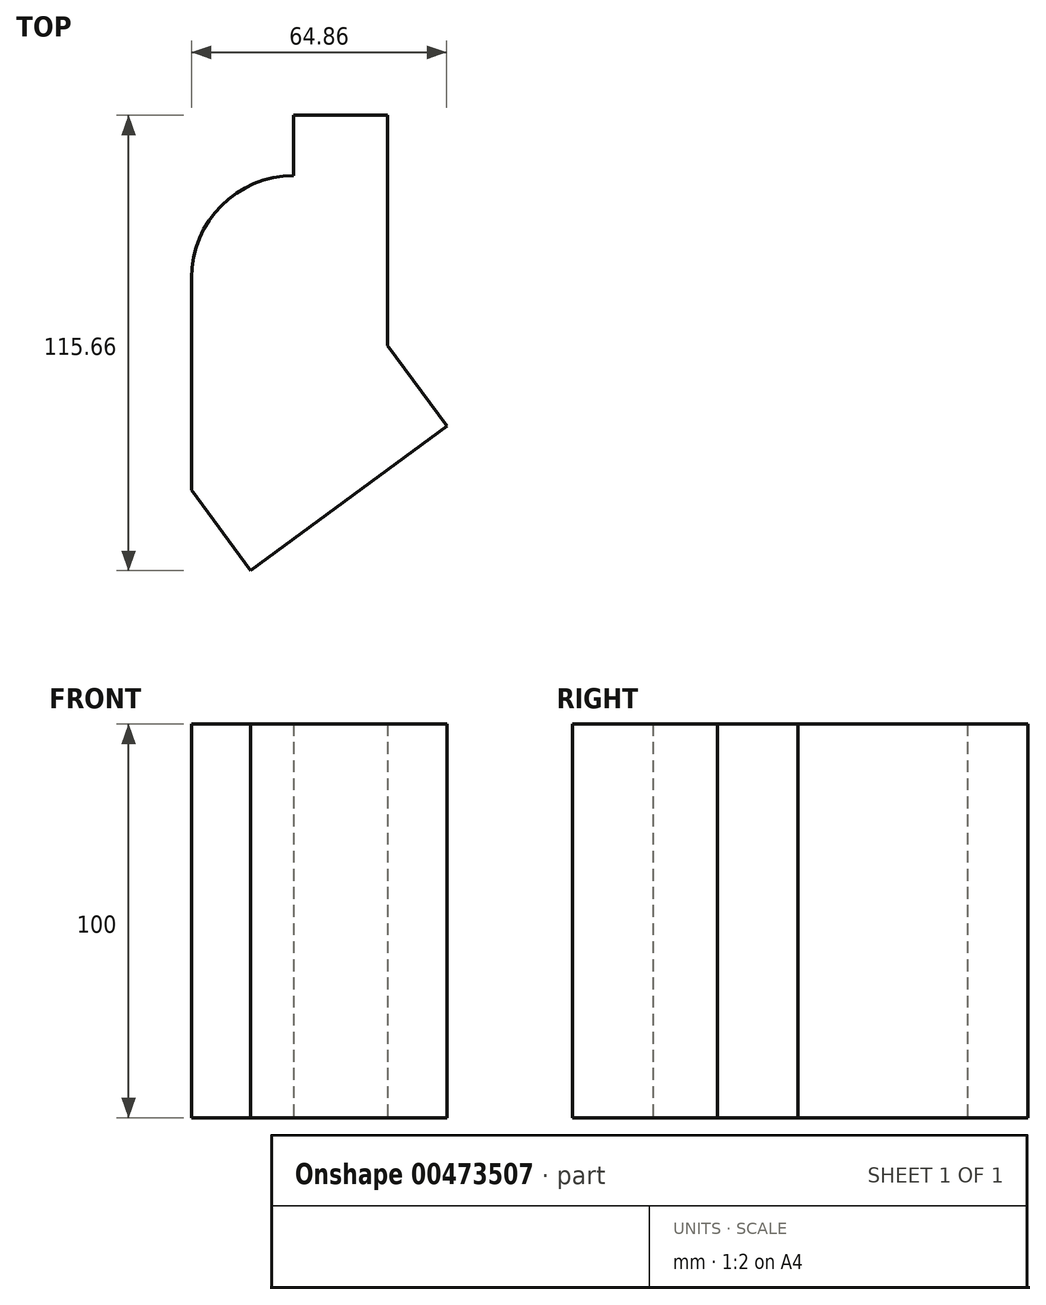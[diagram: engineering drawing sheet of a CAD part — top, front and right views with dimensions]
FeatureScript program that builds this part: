
annotation { "Feature Type Name" : "Feature", "Feature Type Description" : "" }
export const myFeature = defineFeature(function(context is Context, id is Id, definition is map)
    precondition{}
    {
        {
            var Q0;
            Q0=qCreatedBy(makeId("Top.planeOp"),FACE);
            var sketch = newSketch(context, id + "F0", { "sketchPlane" : qUnion([Q0])});
            skLineSegment(sketch, "E0", {"start": v(-63.48, -53.94) * mm, "end": v(-63.48, 0) * mm});
            skLineSegment(sketch, "E1", {"start": v(-37.55, 25.93) * mm, "end": v(-37.55, 41.28) * mm});
            skLineSegment(sketch, "E2", {"start": v(-37.55, 41.28) * mm, "end": v(-13.7, 41.28) * mm});
            skLineSegment(sketch, "E3", {"start": v(-13.7, 41.28) * mm, "end": v(-13.7, -17.22) * mm});
            skLineSegment(sketch, "E4", {"start": v(-63.48, -53.94) * mm, "end": v(-13.7, -17.22) * mm});
            skArc(sketch, "E5", {"start": v(-37.55, 25.93) * mm, "mid": v(-55.89, 18.34) * mm, "end": v(-63.48, 0) * mm});
            skSolve(sketch);
        }
        {
            var Q0;
            Q0 = qSketchRegion(id + "F0", true);
            extrude(context, id + "F1", {"entities" : qUnion([Q0]), "depth" : 100 * mm});
        }
        {
            var Q0;
            Q0=makeQuery(id+"F1.opExtrude","SWEPT_FACE",FACE,{"disambiguationData":[OSD([sQuery(id+"F0.wireOp",EDGE,"E4")])]});
            extrude(context, id + "F2", {"entities" : qUnion([Q0]), "operationType" : NewBodyOperationType.ADD, "depth" : 25.4 * mm});
        }
    });
